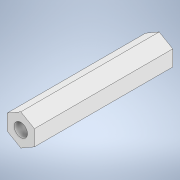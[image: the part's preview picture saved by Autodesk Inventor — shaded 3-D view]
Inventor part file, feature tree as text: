
AUTODESK INVENTOR PART (.ipt)
format: ipt  version: 2022 (Build 260153000, 153)  size: 97,792 bytes
history: native  units: mm
features: other x1, extrude x1, sketch x1
ambient origin geometry x8: Origin, YZ Plane, XZ Plane, XY Plane, X Axis, Y Axis, Z Axis, Center Point
bodies: Body1 (feature_tree)
feature tree (3):
  other  "ソリッド1"
  extrude  "押し出し1"  Depth=5.5mm
  sketch  "スケッチ1"
